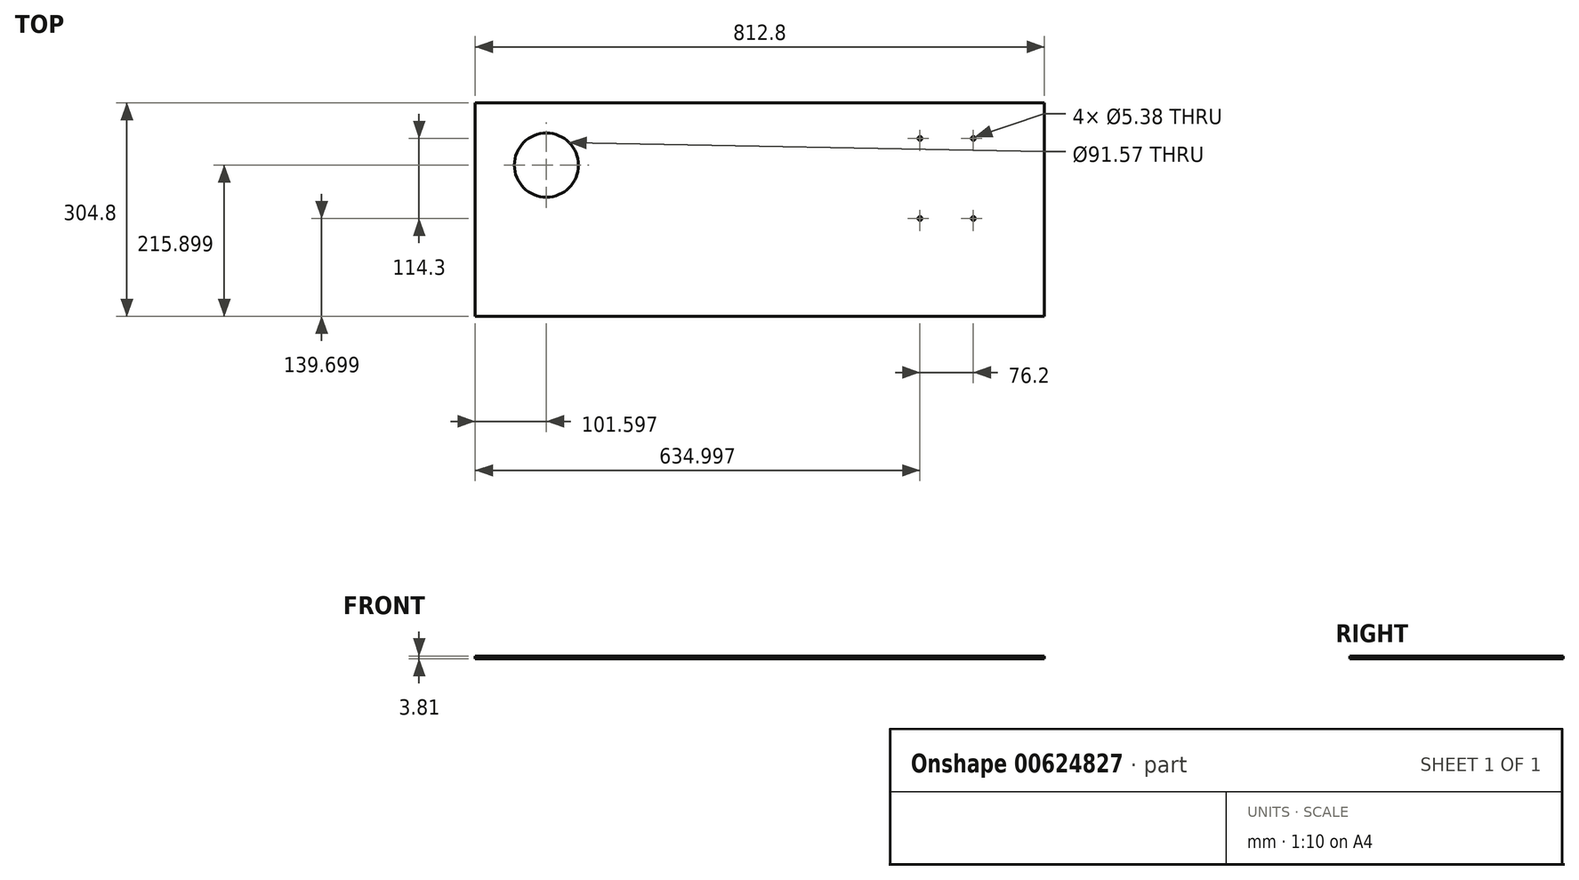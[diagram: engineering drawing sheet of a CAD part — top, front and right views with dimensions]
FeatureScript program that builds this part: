
annotation { "Feature Type Name" : "Feature", "Feature Type Description" : "" }
export const myFeature = defineFeature(function(context is Context, id is Id, definition is map)
    precondition{}
    {
        {
            var Q0;
            Q0=qCreatedBy(makeId("Top.planeOp"),FACE);
            var sketch = newSketch(context, id + "F0", { "sketchPlane" : qUnion([Q0])});
            skLineSegment(sketch, "E0.bottom", {"start": v(-91.56, 356.04) * mm, "end": v(721.24, 356.04) * mm});
            skLineSegment(sketch, "E0.top", {"start": v(-91.56, 51.24) * mm, "end": v(721.24, 51.24) * mm});
            skLineSegment(sketch, "E0.left", {"start": v(-91.56, 356.04) * mm, "end": v(-91.56, 51.24) * mm});
            skLineSegment(sketch, "E0.right", {"start": v(721.24, 356.04) * mm, "end": v(721.24, 51.24) * mm});
            skPoint(sketch, "E1", {"position": v(10.04, 267.14) * mm});
            skCircle(sketch, "E2", {"center": v(10.04, 267.14) * mm, "radius": 45.78 * mm});
            skCircle(sketch, "E3", {"center": v(543.44, 305.24) * mm, "radius": 2.7 * mm});
            skCircle(sketch, "E4", {"center": v(619.64, 305.24) * mm, "radius": 2.7 * mm});
            skCircle(sketch, "E5", {"center": v(543.44, 190.94) * mm, "radius": 2.7 * mm});
            skCircle(sketch, "E6", {"center": v(619.64, 190.94) * mm, "radius": 2.7 * mm});
            skSolve(sketch);
        }
        {
            var Q0;
            Q0=makeQuery(id+"F0.imprint","IMPRINT",FACE,{"disambiguationData":[TD([[makeQuery(id+"F0.imprint","IMPRINT",EDGE,{"derivedFrom":sQuery(id+"F0.wireOp",EDGE,"E0.bottom")}),-1.0]])]});
            extrude(context, id + "F1", {"entities" : qUnion([Q0]), "depth" : 3.8 * mm, "offsetDistance" : 25.4 * mm});
        }
    });
